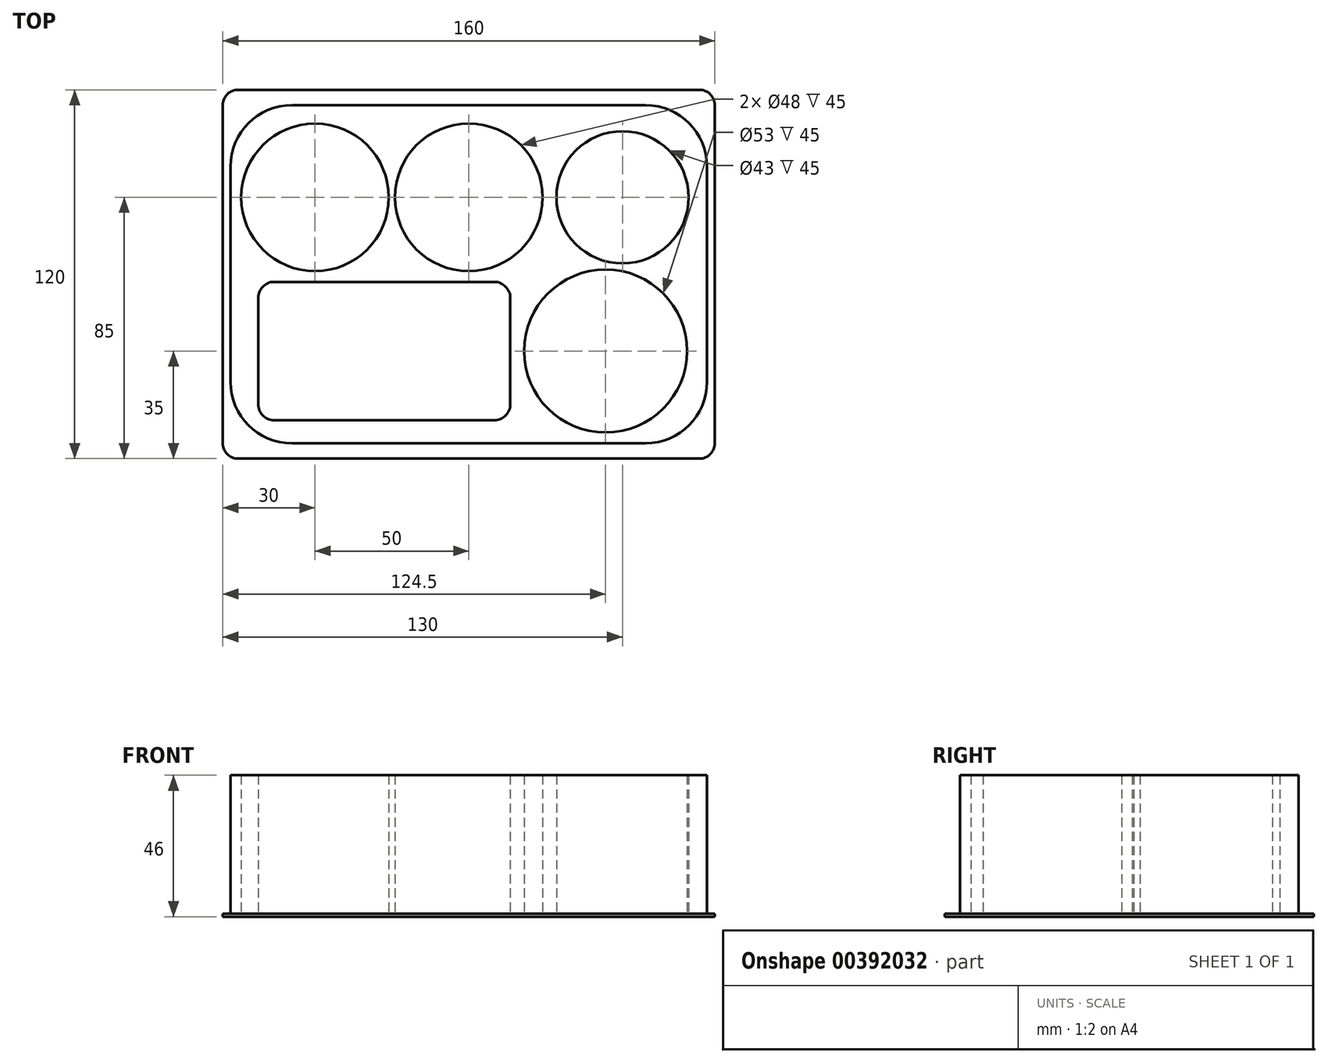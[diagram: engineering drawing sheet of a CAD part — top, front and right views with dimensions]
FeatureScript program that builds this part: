
annotation { "Feature Type Name" : "Feature", "Feature Type Description" : "" }
export const myFeature = defineFeature(function(context is Context, id is Id, definition is map)
    precondition{}
    {
        {
            var Q0;
            Q0=qCreatedBy(makeId("Top.planeOp"),FACE);
            var sketch = newSketch(context, id + "F0", { "sketchPlane" : qUnion([Q0])});
            skLineSegment(sketch, "E0.bottom", {"start": v(77.5, 55) * mm, "end": v(-77.5, 55) * mm});
            skLineSegment(sketch, "E0.top", {"start": v(77.5, -55) * mm, "end": v(-77.5, -55) * mm});
            skLineSegment(sketch, "E0.left", {"start": v(77.5, 55) * mm, "end": v(77.5, -55) * mm});
            skLineSegment(sketch, "E0.right", {"start": v(-77.5, 55) * mm, "end": v(-77.5, -55) * mm});
            skPoint(sketch, "E0.middle", {"position": v(0, 0) * mm});
            skCircle(sketch, "E1", {"center": v(-50, 25) * mm, "radius": 24 * mm});
            skCircle(sketch, "E2", {"center": v(0, 25) * mm, "radius": 24 * mm});
            skCircle(sketch, "E3", {"center": v(50, 25) * mm, "radius": 21.5 * mm});
            skLineSegment(sketch, "E4", {"start": v(-50, 25) * mm, "end": v(-50, 55) * mm, "construction": true});
            skLineSegment(sketch, "E5", {"start": v(0, 25) * mm, "end": v(0, 55) * mm, "construction": true});
            skLineSegment(sketch, "E6", {"start": v(50, 25) * mm, "end": v(50, 55) * mm, "construction": true});
            skCircle(sketch, "E7", {"center": v(44.5, -25) * mm, "radius": 26.5 * mm});
            skLineSegment(sketch, "E8.bottom", {"start": v(13.5, -2.5) * mm, "end": v(-68.5, -2.5) * mm});
            skLineSegment(sketch, "E8.top", {"start": v(13.5, -47.5) * mm, "end": v(-68.5, -47.5) * mm});
            skLineSegment(sketch, "E8.left", {"start": v(13.5, -2.5) * mm, "end": v(13.5, -47.5) * mm});
            skLineSegment(sketch, "E8.right", {"start": v(-68.5, -2.5) * mm, "end": v(-68.5, -47.5) * mm});
            skPoint(sketch, "E8.middle", {"position": v(-27.5, -25) * mm});
            skSolve(sketch);
        }
        {
            var Q0;
            Q0 = qSketchRegion(id + "F0", true);
            extrude(context, id + "F1", {"entities" : qUnion([Q0]), "depth" : 45 * mm});
        }
        {
            var Q0;
            Q0=makeQuery(id+"F0.imprint","IMPRINT",FACE,{"disambiguationData":[TD([[makeQuery(id+"F0.imprint","IMPRINT",EDGE,{"derivedFrom":sQuery(id+"F0.wireOp",EDGE,"E0.bottom")}),1.0]])]});
            var sketch = newSketch(context, id + "F2", { "sketchPlane" : qUnion([Q0])});
            skLineSegment(sketch, "E9.bottom", {"start": v(-80, -60) * mm, "end": v(80, -60) * mm});
            skLineSegment(sketch, "E9.top", {"start": v(-80, 60) * mm, "end": v(80, 60) * mm});
            skLineSegment(sketch, "E9.left", {"start": v(-80, -60) * mm, "end": v(-80, 60) * mm});
            skLineSegment(sketch, "E9.right", {"start": v(80, -60) * mm, "end": v(80, 60) * mm});
            skPoint(sketch, "E9.middle", {"position": v(0, 0) * mm});
            skSolve(sketch);
        }
        {
            var Q0;
            Q0=makeQuery(id+"F2.imprint","IMPRINT",FACE,{"disambiguationData":[TD([[makeQuery(id+"F2.imprint","IMPRINT",EDGE,{"derivedFrom":sQuery(id+"F2.wireOp",EDGE,"E9.bottom")}),1.0]])]});
            var Q1;
            Q1=makeQuery(id+"F0.imprint","IMPRINT",FACE,{"disambiguationData":[TD([[makeQuery(id+"F0.imprint","IMPRINT",EDGE,{"derivedFrom":sQuery(id+"F0.wireOp",EDGE,"E8.bottom")}),1.0]])]});
            var Q2;
            Q2=makeQuery(id+"F0.imprint","IMPRINT",FACE,{"disambiguationData":[TD([[makeQuery(id+"F0.imprint","IMPRINT",EDGE,{"derivedFrom":sQuery(id+"F0.wireOp",EDGE,"E0.bottom")}),1.0]])]});
            var Q3;
            Q3=makeQuery(id+"F0.imprint","IMPRINT",FACE,{"disambiguationData":[TD([[makeQuery(id+"F0.imprint","IMPRINT",EDGE,{"derivedFrom":sQuery(id+"F0.wireOp",EDGE,"E7")}),1.0]])]});
            var Q4;
            Q4=makeQuery(id+"F0.imprint","IMPRINT",FACE,{"disambiguationData":[TD([[makeQuery(id+"F0.imprint","IMPRINT",EDGE,{"derivedFrom":sQuery(id+"F0.wireOp",EDGE,"E3")}),1.0]])]});
            var Q5;
            Q5=makeQuery(id+"F0.imprint","IMPRINT",FACE,{"disambiguationData":[TD([[makeQuery(id+"F0.imprint","IMPRINT",EDGE,{"derivedFrom":sQuery(id+"F0.wireOp",EDGE,"E2")}),1.0]])]});
            var Q6;
            Q6=makeQuery(id+"F0.imprint","IMPRINT",FACE,{"disambiguationData":[TD([[makeQuery(id+"F0.imprint","IMPRINT",EDGE,{"derivedFrom":sQuery(id+"F0.wireOp",EDGE,"E1")}),1.0]])]});
            extrude(context, id + "F3", {"entities" : qUnion([Q0, Q1, Q2, Q3, Q4, Q5, Q6]), "operationType" : NewBodyOperationType.ADD, "oppositeDirection" : true, "depth" : 1 * mm});
        }
        {
            var Q0;
            Q0=makeQuery(id+"F3.opExtrude","SWEPT_EDGE",EDGE,{"disambiguationData":[OSD([sQuery(id+"F2.wireOp",EDGE,"E9.bottom"),sQuery(id+"F2.wireOp",EDGE,"E9.left")])]});
            var Q1;
            Q1=makeQuery(id+"F3.opExtrude","SWEPT_EDGE",EDGE,{"disambiguationData":[OSD([sQuery(id+"F2.wireOp",EDGE,"E9.top"),sQuery(id+"F2.wireOp",EDGE,"E9.left")])]});
            var Q2;
            Q2=makeQuery(id+"F3.opExtrude","SWEPT_EDGE",EDGE,{"disambiguationData":[OSD([sQuery(id+"F2.wireOp",EDGE,"E9.top"),sQuery(id+"F2.wireOp",EDGE,"E9.right")])]});
            var Q3;
            Q3=makeQuery(id+"F3.opExtrude","SWEPT_EDGE",EDGE,{"disambiguationData":[OSD([sQuery(id+"F2.wireOp",EDGE,"E9.bottom"),sQuery(id+"F2.wireOp",EDGE,"E9.right")])]});
            fillet(context, id + "F4", {"entities" : qUnion([Q0, Q1, Q2, Q3]), "radius" : 5 * mm, "tangentPropagation" : true, "allowEdgeOverflow" : false});
        }
        {
            var Q0;
            Q0=makeQuery(id+"F1.opExtrude","SWEPT_EDGE",EDGE,{"disambiguationData":[OSD([sQuery(id+"F0.wireOp",EDGE,"E0.top"),sQuery(id+"F0.wireOp",EDGE,"E0.left")])]});
            var Q1;
            Q1=makeQuery(id+"F1.opExtrude","SWEPT_EDGE",EDGE,{"disambiguationData":[OSD([sQuery(id+"F0.wireOp",EDGE,"E0.top"),sQuery(id+"F0.wireOp",EDGE,"E0.right")])]});
            var Q2;
            Q2=makeQuery(id+"F1.opExtrude","SWEPT_EDGE",EDGE,{"disambiguationData":[OSD([sQuery(id+"F0.wireOp",EDGE,"E0.bottom"),sQuery(id+"F0.wireOp",EDGE,"E0.right")])]});
            var Q3;
            Q3=makeQuery(id+"F1.opExtrude","SWEPT_EDGE",EDGE,{"disambiguationData":[OSD([sQuery(id+"F0.wireOp",EDGE,"E0.bottom"),sQuery(id+"F0.wireOp",EDGE,"E0.left")])]});
            fillet(context, id + "F5", {"entities" : qUnion([Q0, Q1, Q2, Q3]), "radius" : 20 * mm, "tangentPropagation" : true, "allowEdgeOverflow" : false});
        }
        {
            var Q0;
            Q0=makeQuery(id+"F1.opExtrude","SWEPT_EDGE",EDGE,{"disambiguationData":[OSD([sQuery(id+"F0.wireOp",EDGE,"E8.top"),sQuery(id+"F0.wireOp",EDGE,"E8.right")])]});
            var Q1;
            Q1=makeQuery(id+"F1.opExtrude","SWEPT_EDGE",EDGE,{"disambiguationData":[OSD([sQuery(id+"F0.wireOp",EDGE,"E8.bottom"),sQuery(id+"F0.wireOp",EDGE,"E8.right")])]});
            var Q2;
            Q2=makeQuery(id+"F1.opExtrude","SWEPT_EDGE",EDGE,{"disambiguationData":[OSD([sQuery(id+"F0.wireOp",EDGE,"E8.bottom"),sQuery(id+"F0.wireOp",EDGE,"E8.left")])]});
            var Q3;
            Q3=makeQuery(id+"F1.opExtrude","SWEPT_EDGE",EDGE,{"disambiguationData":[OSD([sQuery(id+"F0.wireOp",EDGE,"E8.top"),sQuery(id+"F0.wireOp",EDGE,"E8.left")])]});
            fillet(context, id + "F6", {"entities" : qUnion([Q0, Q1, Q2, Q3]), "radius" : 5.2 * mm, "tangentPropagation" : true, "allowEdgeOverflow" : false});
        }
    });
